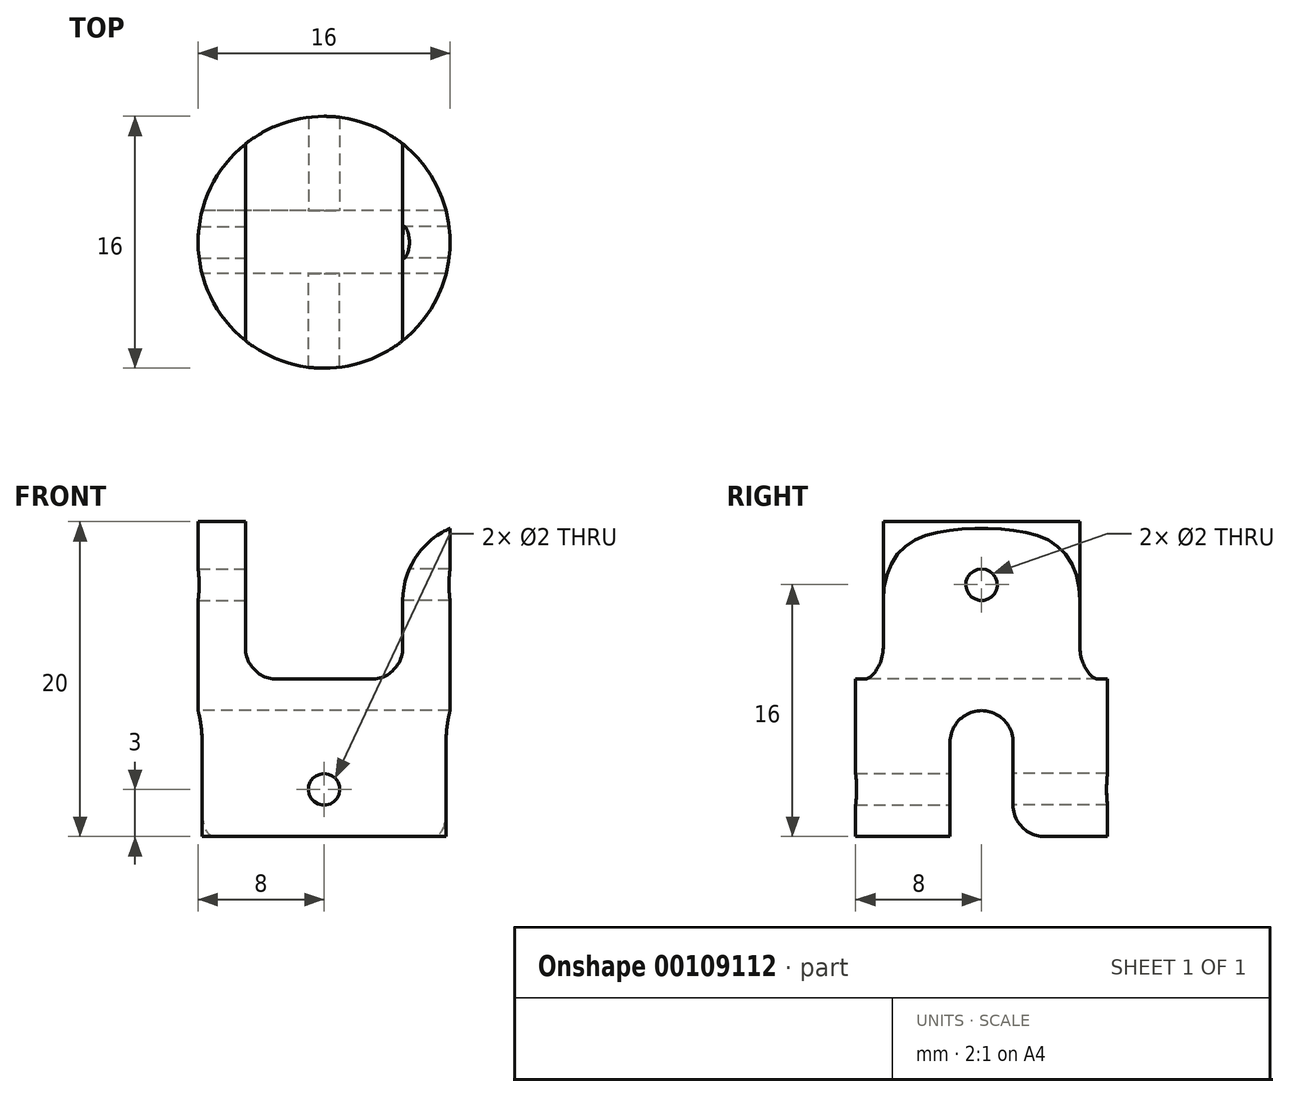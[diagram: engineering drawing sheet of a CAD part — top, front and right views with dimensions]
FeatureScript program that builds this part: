
annotation { "Feature Type Name" : "Feature", "Feature Type Description" : "" }
export const myFeature = defineFeature(function(context is Context, id is Id, definition is map)
    precondition{}
    {
        {
            var Q0;
            Q0=qCreatedBy(makeId("Top.planeOp"),FACE);
            var sketch = newSketch(context, id + "F0", { "sketchPlane" : qUnion([Q0])});
            skCircle(sketch, "E0", {"center": v(0, 0) * mm, "radius": 8 * mm});
            skSolve(sketch);
        }
        {
            var Q0;
            Q0=makeQuery(id+"F0.imprint","IMPRINT",FACE,{"disambiguationData":[TD([[makeQuery(id+"F0.imprint","IMPRINT",EDGE,{"derivedFrom":sQuery(id+"F0.wireOp",EDGE,"E0")}),1.0]])]});
            extrude(context, id + "F1", {"entities" : qUnion([Q0]), "depth" : 20 * mm});
        }
        {
            var Q0;
            Q0=makeQuery(id+"F1.opExtrude","CAP_FACE",FACE,{"disambiguationData":[OSD([sQuery(id+"F0.wireOp",EDGE,"E0")])],"isStart":false});
            var sketch = newSketch(context, id + "F2", { "sketchPlane" : qUnion([Q0])});
            skLineSegment(sketch, "E1", {"start": v(-5, 6.24) * mm, "end": v(-5, -6.24) * mm});
            skLineSegment(sketch, "E2", {"start": v(5, 6.24) * mm, "end": v(5, -6.24) * mm});
            skSolve(sketch);
        }
        {
            var Q0;
            {var subQ0=sQuery(id+"F2.wireOp",EDGE,"E1");Q0=makeQuery(id+"F2.imprint","IMPRINT",FACE,{"disambiguationData":[TD([[makeQuery(id+"F2.imprint","IMPRINT",EDGE,{"derivedFrom":subQ0}),1.0]])]});}
            extrude(context, id + "F3", {"entities" : qUnion([Q0]), "operationType" : NewBodyOperationType.REMOVE, "oppositeDirection" : true, "depth" : 10 * mm});
        }
        {
            var Q0;
            Q0=makeQuery(id+"F0.imprint","IMPRINT",FACE,{"disambiguationData":[TD([[makeQuery(id+"F0.imprint","IMPRINT",EDGE,{"derivedFrom":sQuery(id+"F0.wireOp",EDGE,"E0")}),1.0]])]});
            var sketch = newSketch(context, id + "F4", { "sketchPlane" : qUnion([Q0])});
            skLineSegment(sketch, "E3.bottom", {"start": v(8, 2) * mm, "end": v(-8, 2) * mm});
            skLineSegment(sketch, "E3.top", {"start": v(8, -2) * mm, "end": v(-8, -2) * mm});
            skLineSegment(sketch, "E3.left", {"start": v(8, 2) * mm, "end": v(8, -2) * mm});
            skLineSegment(sketch, "E3.right", {"start": v(-8, 2) * mm, "end": v(-8, -2) * mm});
            skPoint(sketch, "E3.middle", {"position": v(0, 0) * mm});
            skSolve(sketch);
        }
        {
            var Q0;
            {var subQ0=sQuery(id+"F4.wireOp",EDGE,"E3.bottom");var subQ1=makeQuery(id+"F0.imprint","IMPRINT",EDGE,{"derivedFrom":sQuery(id+"F0.wireOp",EDGE,"E0")});var subQ4=makeQuery(id+"F4.imprint","INTERSECT",VERTEX,{"disambiguationData":[OD(0.0)],"derivedFrom":[subQ1,subQ0]});Q0=makeQuery(id+"F4.imprint","IMPRINT",FACE,{"disambiguationData":[TD([[makeQuery(id+"F4.imprint","IMPRINT",EDGE,{"disambiguationData":[TD([[subQ4,-1.0]])],"derivedFrom":subQ0}),1.0]])]});}
            extrude(context, id + "F5", {"entities" : qUnion([Q0]), "operationType" : NewBodyOperationType.REMOVE, "depth" : 8 * mm});
        }
        {
            var Q0;
            Q0=makeQuery(id+"F3.boolean.opBoolean","COPY",FACE,{"derivedFrom":makeQuery(id+"F3.opExtrude","SWEPT_FACE",FACE,{"disambiguationData":[OSD([sQuery(id+"F2.wireOp",EDGE,"E1")])]})});
            var sketch = newSketch(context, id + "F6", { "sketchPlane" : qUnion([Q0])});
            skCircle(sketch, "E4", {"center": v(0, 16) * mm, "radius": 1 * mm});
            skSolve(sketch);
        }
        {
            var Q0;
            Q0=sQuery(id+"F6.wireOp",VERTEX,"E4.center");
            var Q1;
            Q1=makeQuery(id+"F1.opExtrude","SWEPT_BODY",BODY,{"disambiguationData":[OSD([sQuery(id+"F0.wireOp",EDGE,"E0")])]});
            hole(context, id + "F7", {"style" : HoleStyle.SIMPLE, "endStyle" : HoleEndStyle.THROUGH, "holeDiameter" : 2 * mm, "locations" : qUnion([Q0]), "scope" : qUnion([Q1]), "isTappedThrough" : true});
        }
        {
            var Q0;
            Q0=makeQuery(id+"F3.boolean.opBoolean","COPY",FACE,{"derivedFrom":makeQuery(id+"F3.opExtrude","SWEPT_FACE",FACE,{"disambiguationData":[OSD([sQuery(id+"F2.wireOp",EDGE,"E2")])]})});
            var sketch = newSketch(context, id + "F8", { "sketchPlane" : qUnion([Q0])});
            skCircle(sketch, "E5", {"center": v(0, 16) * mm, "radius": 1 * mm});
            skSolve(sketch);
        }
        {
            var Q0;
            Q0=sQuery(id+"F8.wireOp",VERTEX,"E5.center");
            var Q1;
            Q1=makeQuery(id+"F1.opExtrude","SWEPT_BODY",BODY,{"disambiguationData":[OSD([sQuery(id+"F0.wireOp",EDGE,"E0")])]});
            hole(context, id + "F9", {"style" : HoleStyle.SIMPLE, "endStyle" : HoleEndStyle.THROUGH, "holeDiameter" : 2 * mm, "locations" : qUnion([Q0]), "scope" : qUnion([Q1]), "isTappedThrough" : true});
        }
        {
            var Q0;
            Q0=makeQuery(id+"F3.boolean.opBoolean","COPY",EDGE,{"derivedFrom":makeQuery(id+"F3.opExtrude","CAP_EDGE",EDGE,{"disambiguationData":[OSD([sQuery(id+"F2.wireOp",EDGE,"E2")])],"isStart":true})});
            var Q1;
            Q1=makeQuery(id+"F3.boolean.opBoolean","COPY",EDGE,{"derivedFrom":makeQuery(id+"F3.opExtrude","CAP_EDGE",EDGE,{"disambiguationData":[OSD([sQuery(id+"F2.wireOp",EDGE,"E1")])],"isStart":true})});
            fillet(context, id + "F10", {"entities" : qUnion([Q0, Q1]), "radius" : 5 * mm, "tangentPropagation" : true, "allowEdgeOverflow" : false});
        }
        {
            var Q0;
            Q0=makeQuery(id+"F5.boolean.opBoolean","COPY",FACE,{"derivedFrom":makeQuery(id+"F5.opExtrude","SWEPT_FACE",FACE,{"disambiguationData":[OSD([sQuery(id+"F4.wireOp",EDGE,"E3.top")])]})});
            var sketch = newSketch(context, id + "F11", { "sketchPlane" : qUnion([Q0])});
            skCircle(sketch, "E6", {"center": v(0, 3) * mm, "radius": 1 * mm});
            skSolve(sketch);
        }
        {
            var Q0;
            Q0=sQuery(id+"F11.wireOp",VERTEX,"E6.center");
            var Q1;
            Q1=makeQuery(id+"F1.opExtrude","SWEPT_BODY",BODY,{"disambiguationData":[OSD([sQuery(id+"F0.wireOp",EDGE,"E0")])]});
            hole(context, id + "F12", {"style" : HoleStyle.SIMPLE, "endStyle" : HoleEndStyle.THROUGH, "holeDiameter" : 2 * mm, "locations" : qUnion([Q0]), "scope" : qUnion([Q1]), "isTappedThrough" : true});
        }
        {
            var Q0;
            Q0=makeQuery(id+"F5.boolean.opBoolean","COPY",FACE,{"derivedFrom":makeQuery(id+"F5.opExtrude","SWEPT_FACE",FACE,{"disambiguationData":[OSD([sQuery(id+"F4.wireOp",EDGE,"E3.bottom")])]})});
            var sketch = newSketch(context, id + "F13", { "sketchPlane" : qUnion([Q0])});
            skCircle(sketch, "E7", {"center": v(0, 3) * mm, "radius": 1 * mm});
            skSolve(sketch);
        }
        {
            var Q0;
            Q0=sQuery(id+"F13.wireOp",VERTEX,"E7.center");
            var Q1;
            Q1=makeQuery(id+"F1.opExtrude","SWEPT_BODY",BODY,{"disambiguationData":[OSD([sQuery(id+"F0.wireOp",EDGE,"E0")])]});
            hole(context, id + "F14", {"style" : HoleStyle.SIMPLE, "endStyle" : HoleEndStyle.THROUGH, "holeDiameter" : 2 * mm, "locations" : qUnion([Q0]), "scope" : qUnion([Q1]), "isTappedThrough" : true});
        }
        {
            var Q0;
            Q0=makeQuery(id+"F5.boolean.opBoolean","COPY",EDGE,{"derivedFrom":makeQuery(id+"F5.opExtrude","CAP_EDGE",EDGE,{"disambiguationData":[OSD([sQuery(id+"F4.wireOp",EDGE,"E3.bottom")])],"isStart":true})});
            var Q1;
            Q1=makeQuery(id+"F5.boolean.opBoolean","COPY",EDGE,{"derivedFrom":makeQuery(id+"F5.opExtrude","CAP_EDGE",EDGE,{"disambiguationData":[OSD([sQuery(id+"F4.wireOp",EDGE,"E3.top")])],"isStart":true})});
            fillet(context, id + "F15", {"entities" : qUnion([Q0, Q1]), "radius" : 2 * mm, "tangentPropagation" : true, "allowEdgeOverflow" : false});
        }
        {
            var Q0;
            Q0=makeQuery(id+"F3.boolean.opBoolean","COPY",EDGE,{"derivedFrom":makeQuery(id+"F3.opExtrude","CAP_EDGE",EDGE,{"disambiguationData":[OSD([sQuery(id+"F2.wireOp",EDGE,"E1")])],"isStart":false})});
            var Q1;
            Q1=makeQuery(id+"F3.boolean.opBoolean","COPY",EDGE,{"derivedFrom":makeQuery(id+"F3.opExtrude","CAP_EDGE",EDGE,{"disambiguationData":[OSD([sQuery(id+"F2.wireOp",EDGE,"E2")])],"isStart":false})});
            var Q2;
            Q2=makeQuery(id+"F5.boolean.opBoolean","COPY",EDGE,{"derivedFrom":makeQuery(id+"F5.opExtrude","CAP_EDGE",EDGE,{"disambiguationData":[OSD([sQuery(id+"F4.wireOp",EDGE,"E3.bottom")])],"isStart":false})});
            var Q3;
            Q3=makeQuery(id+"F5.boolean.opBoolean","COPY",EDGE,{"derivedFrom":makeQuery(id+"F5.opExtrude","CAP_EDGE",EDGE,{"disambiguationData":[OSD([sQuery(id+"F4.wireOp",EDGE,"E3.top")])],"isStart":false})});
            fillet(context, id + "F16", {"entities" : qUnion([Q0, Q1, Q2, Q3]), "radius" : 2 * mm, "tangentPropagation" : true, "allowEdgeOverflow" : false});
        }
    });
